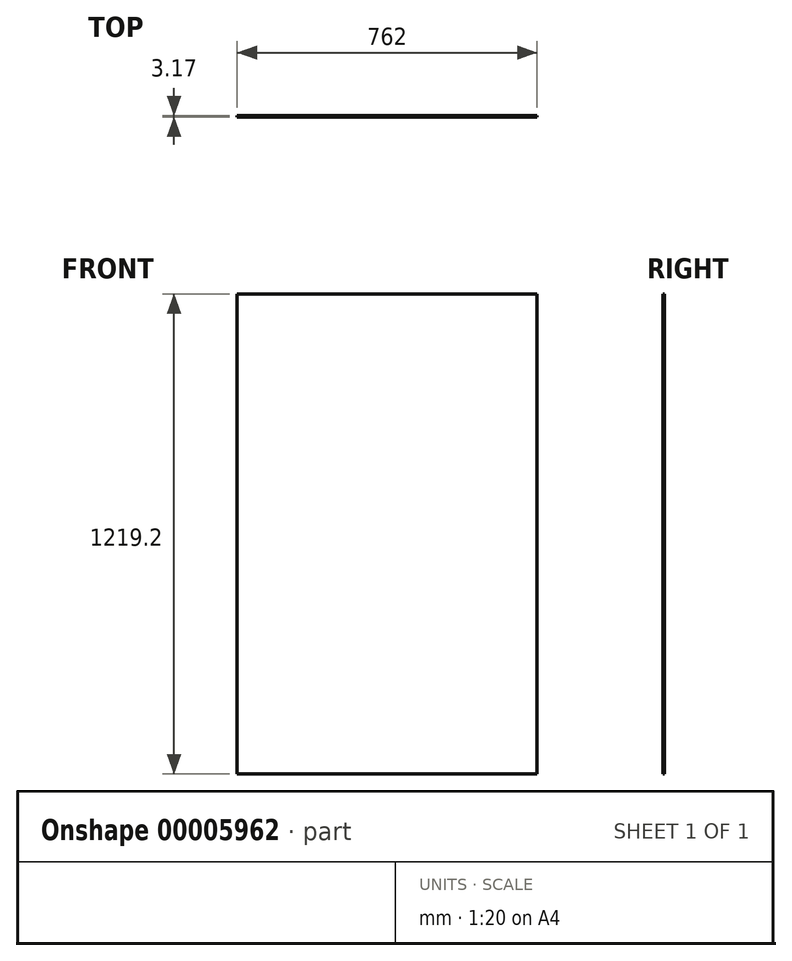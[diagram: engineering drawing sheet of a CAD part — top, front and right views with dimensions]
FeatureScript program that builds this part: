
annotation { "Feature Type Name" : "Feature", "Feature Type Description" : "" }
export const myFeature = defineFeature(function(context is Context, id is Id, definition is map)
    precondition{}
    {
        {
            var Q0;
            Q0=qCreatedBy(makeId("Front.planeOp"),FACE);
            var sketch = newSketch(context, id + "F0", { "sketchPlane" : qUnion([Q0])});
            skLineSegment(sketch, "E0.bottom", {"start": v(-424.22, 536.33) * mm, "end": v(337.78, 536.33) * mm});
            skLineSegment(sketch, "E0.top", {"start": v(-424.22, -682.87) * mm, "end": v(337.78, -682.87) * mm});
            skLineSegment(sketch, "E0.left", {"start": v(-424.22, 536.33) * mm, "end": v(-424.22, -682.87) * mm});
            skLineSegment(sketch, "E0.right", {"start": v(337.78, 536.33) * mm, "end": v(337.78, -682.87) * mm});
            skSolve(sketch);
        }
        {
            var Q0;
            Q0=qSketchRegion(id+"F0",true);
            extrude(context, id + "F1", {"entities" : qUnion([Q0]), "depth" : 3.17 * mm});
        }
    });
